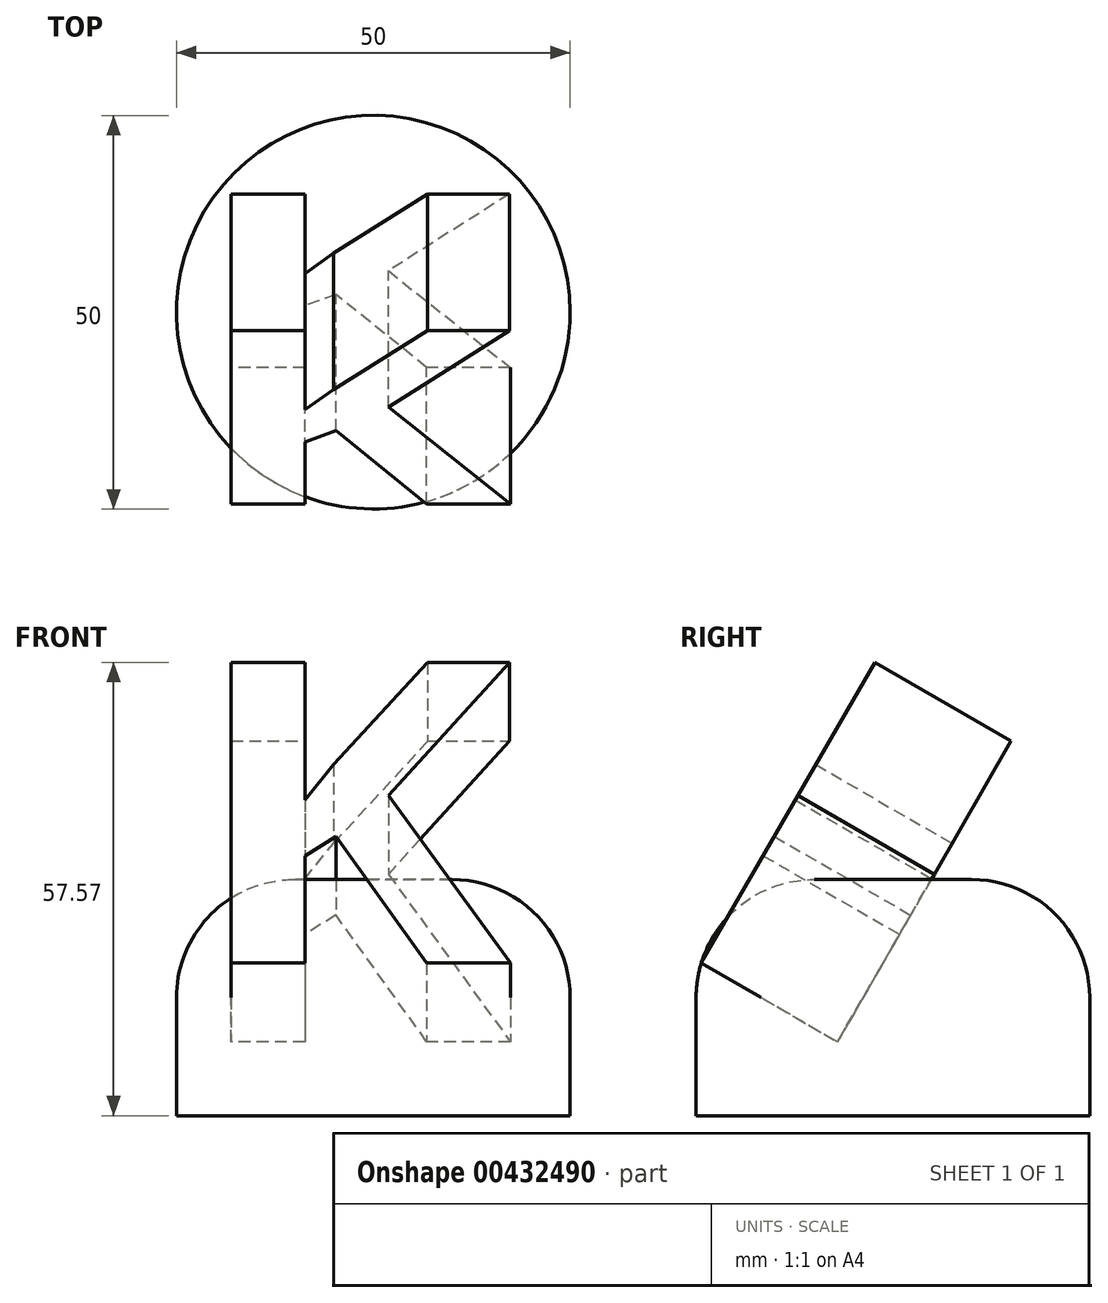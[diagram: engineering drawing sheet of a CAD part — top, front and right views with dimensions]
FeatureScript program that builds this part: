
annotation { "Feature Type Name" : "Feature", "Feature Type Description" : "" }
export const myFeature = defineFeature(function(context is Context, id is Id, definition is map)
    precondition{}
    {
        {
            var Q0;
            Q0=qCreatedBy(makeId("Top.planeOp"),FACE);
            var sketch = newSketch(context, id + "F0", { "sketchPlane" : qUnion([Q0])});
            skText(sketch, "E0", { "text": "K", "fontName": "OpenSans-Bold.ttf"});
            const initialGuessF0  = {"E0": [-0.09905, -0.02622, 1, 0, 0.04445]};
            skSetInitialGuess(sketch, initialGuessF0);
            skSolve(sketch);
        }
        {
            var Q0;
            Q0=qSketchRegion(id+"F0",true);
            extrude(context, id + "F1", {"entities" : qUnion([Q0]), "depth" : 20 * mm});
        }
        {
            var Q0;
            Q0=makeQuery(id+"F1.opExtrude","SWEPT_BODY",BODY,{"disambiguationData":[OSD([sQuery(id+"F0.wireOp",EDGE,"E0.sketch_text.stroke-0"),sQuery(id+"F0.wireOp",EDGE,"E0.sketch_text.stroke-1"),sQuery(id+"F0.wireOp",EDGE,"E0.sketch_text.stroke-2"),sQuery(id+"F0.wireOp",EDGE,"E0.sketch_text.stroke-3"),sQuery(id+"F0.wireOp",EDGE,"E0.sketch_text.stroke-4"),sQuery(id+"F0.wireOp",EDGE,"E0.sketch_text.stroke-5"),sQuery(id+"F0.wireOp",EDGE,"E0.sketch_text.stroke-6"),sQuery(id+"F0.wireOp",EDGE,"E0.sketch_text.stroke-7"),sQuery(id+"F0.wireOp",EDGE,"E0.sketch_text.stroke-8"),sQuery(id+"F0.wireOp",EDGE,"E0.sketch_text.stroke-9"),sQuery(id+"F0.wireOp",EDGE,"E0.sketch_text.stroke-10"),sQuery(id+"F0.wireOp",EDGE,"E0.sketch_text.stroke-11"),sQuery(id+"F0.wireOp",EDGE,"E0.sketch_text.stroke-12"),sQuery(id+"F0.wireOp",EDGE,"E0.sketch_text.stroke-13")])]});
            transform(context, id + "F2", {"entities" : qUnion([Q0]), "transformType" : TransformType.TRANSLATION_3D, "dx" : 76.45 * mm, "dy" : 0 * mm, "dz" : 0 * mm, "makeCopy" : false});
        }
        {
            var Q0;
            Q0=qCreatedBy(makeId("Top.planeOp"),FACE);
            var sketch = newSketch(context, id + "F3", { "sketchPlane" : qUnion([Q0])});
            skCircle(sketch, "E1", {"center": v(-27.2, 27.91) * mm, "radius": 25 * mm});
            skSolve(sketch);
        }
        {
            var Q0;
            Q0=makeQuery(id+"F1.opExtrude","SWEPT_BODY",BODY,{"disambiguationData":[OSD([sQuery(id+"F0.wireOp",EDGE,"E0.sketch_text.stroke-0"),sQuery(id+"F0.wireOp",EDGE,"E0.sketch_text.stroke-1"),sQuery(id+"F0.wireOp",EDGE,"E0.sketch_text.stroke-2"),sQuery(id+"F0.wireOp",EDGE,"E0.sketch_text.stroke-3"),sQuery(id+"F0.wireOp",EDGE,"E0.sketch_text.stroke-4"),sQuery(id+"F0.wireOp",EDGE,"E0.sketch_text.stroke-5"),sQuery(id+"F0.wireOp",EDGE,"E0.sketch_text.stroke-6"),sQuery(id+"F0.wireOp",EDGE,"E0.sketch_text.stroke-7"),sQuery(id+"F0.wireOp",EDGE,"E0.sketch_text.stroke-8"),sQuery(id+"F0.wireOp",EDGE,"E0.sketch_text.stroke-9"),sQuery(id+"F0.wireOp",EDGE,"E0.sketch_text.stroke-10"),sQuery(id+"F0.wireOp",EDGE,"E0.sketch_text.stroke-11"),sQuery(id+"F0.wireOp",EDGE,"E0.sketch_text.stroke-12"),sQuery(id+"F0.wireOp",EDGE,"E0.sketch_text.stroke-13")])]});
            transform(context, id + "F4", {"entities" : qUnion([Q0]), "transformType" : TransformType.TRANSLATION_3D, "dx" : 27.3 * mm, "dy" : 0 * mm, "dz" : 0 * mm, "makeCopy" : false});
        }
        {
            var Q0;
            Q0=makeQuery(id+"F3.imprint","IMPRINT",FACE,{"disambiguationData":[TD([[makeQuery(id+"F3.imprint","IMPRINT",EDGE,{"derivedFrom":sQuery(id+"F3.wireOp",EDGE,"E1")}),1.0]])]});
            extrude(context, id + "F5", {"entities" : qUnion([Q0]), "depth" : 30 * mm});
        }
        {
            var Q0;
            Q0=makeQuery(id+"F5.opExtrude","CAP_FACE",FACE,{"disambiguationData":[OSD([sQuery(id+"F3.wireOp",EDGE,"E1")])],"isStart":false});
            fillet(context, id + "F6", {"entities" : qUnion([Q0]), "radius" : 15 * mm, "tangentPropagation" : true, "allowEdgeOverflow" : false});
        }
        {
            var Q0;
            Q0=makeQuery(id+"F1.opExtrude","SWEPT_BODY",BODY,{"disambiguationData":[OSD([sQuery(id+"F0.wireOp",EDGE,"E0.sketch_text.stroke-0"),sQuery(id+"F0.wireOp",EDGE,"E0.sketch_text.stroke-1"),sQuery(id+"F0.wireOp",EDGE,"E0.sketch_text.stroke-2"),sQuery(id+"F0.wireOp",EDGE,"E0.sketch_text.stroke-3"),sQuery(id+"F0.wireOp",EDGE,"E0.sketch_text.stroke-4"),sQuery(id+"F0.wireOp",EDGE,"E0.sketch_text.stroke-5"),sQuery(id+"F0.wireOp",EDGE,"E0.sketch_text.stroke-6"),sQuery(id+"F0.wireOp",EDGE,"E0.sketch_text.stroke-7"),sQuery(id+"F0.wireOp",EDGE,"E0.sketch_text.stroke-8"),sQuery(id+"F0.wireOp",EDGE,"E0.sketch_text.stroke-9"),sQuery(id+"F0.wireOp",EDGE,"E0.sketch_text.stroke-10"),sQuery(id+"F0.wireOp",EDGE,"E0.sketch_text.stroke-11"),sQuery(id+"F0.wireOp",EDGE,"E0.sketch_text.stroke-12"),sQuery(id+"F0.wireOp",EDGE,"E0.sketch_text.stroke-13")])]});
            var Q1;
            Q1=makeQuery(id+"F1.opExtrude","CAP_EDGE",EDGE,{"disambiguationData":[OSD([sQuery(id+"F0.wireOp",EDGE,"E0.sketch_text.stroke-4")])],"isStart":true});
            transform(context, id + "F7", {"entities" : qUnion([Q0]), "transformType" : TransformType.ROTATION, "transformAxis" : qUnion([Q1]), "angle" : 60 * degree, "oppositeDirection" : true, "makeCopy" : false});
        }
        {
            var Q0;
            Q0=makeQuery(id+"F1.opExtrude","SWEPT_BODY",BODY,{"disambiguationData":[OSD([sQuery(id+"F0.wireOp",EDGE,"E0.sketch_text.stroke-0"),sQuery(id+"F0.wireOp",EDGE,"E0.sketch_text.stroke-1"),sQuery(id+"F0.wireOp",EDGE,"E0.sketch_text.stroke-2"),sQuery(id+"F0.wireOp",EDGE,"E0.sketch_text.stroke-3"),sQuery(id+"F0.wireOp",EDGE,"E0.sketch_text.stroke-4"),sQuery(id+"F0.wireOp",EDGE,"E0.sketch_text.stroke-5"),sQuery(id+"F0.wireOp",EDGE,"E0.sketch_text.stroke-6"),sQuery(id+"F0.wireOp",EDGE,"E0.sketch_text.stroke-7"),sQuery(id+"F0.wireOp",EDGE,"E0.sketch_text.stroke-8"),sQuery(id+"F0.wireOp",EDGE,"E0.sketch_text.stroke-9"),sQuery(id+"F0.wireOp",EDGE,"E0.sketch_text.stroke-10"),sQuery(id+"F0.wireOp",EDGE,"E0.sketch_text.stroke-11"),sQuery(id+"F0.wireOp",EDGE,"E0.sketch_text.stroke-12"),sQuery(id+"F0.wireOp",EDGE,"E0.sketch_text.stroke-13")])]});
            transform(context, id + "F8", {"entities" : qUnion([Q0]), "transformType" : TransformType.TRANSLATION_3D, "dx" : -55.2 * mm, "dy" : 47.1 * mm, "dz" : 9.4 * mm, "makeCopy" : false});
        }
        {
            var Q0;
            Q0=makeQuery(id+"F1.opExtrude","SWEPT_BODY",BODY,{"disambiguationData":[OSD([sQuery(id+"F0.wireOp",EDGE,"E0.sketch_text.stroke-0"),sQuery(id+"F0.wireOp",EDGE,"E0.sketch_text.stroke-1"),sQuery(id+"F0.wireOp",EDGE,"E0.sketch_text.stroke-2"),sQuery(id+"F0.wireOp",EDGE,"E0.sketch_text.stroke-3"),sQuery(id+"F0.wireOp",EDGE,"E0.sketch_text.stroke-4"),sQuery(id+"F0.wireOp",EDGE,"E0.sketch_text.stroke-5"),sQuery(id+"F0.wireOp",EDGE,"E0.sketch_text.stroke-6"),sQuery(id+"F0.wireOp",EDGE,"E0.sketch_text.stroke-7"),sQuery(id+"F0.wireOp",EDGE,"E0.sketch_text.stroke-8"),sQuery(id+"F0.wireOp",EDGE,"E0.sketch_text.stroke-9"),sQuery(id+"F0.wireOp",EDGE,"E0.sketch_text.stroke-10"),sQuery(id+"F0.wireOp",EDGE,"E0.sketch_text.stroke-11"),sQuery(id+"F0.wireOp",EDGE,"E0.sketch_text.stroke-12")])]});
            transform(context, id + "F9", {"entities" : qUnion([Q0]), "transformType" : TransformType.TRANSLATION_3D, "dx" : -0.3 * mm, "dy" : 0 * mm, "dz" : 0 * mm, "makeCopy" : false});
        }
    });
